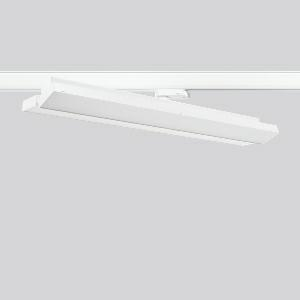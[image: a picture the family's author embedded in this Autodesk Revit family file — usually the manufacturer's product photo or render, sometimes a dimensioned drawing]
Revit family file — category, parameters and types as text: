
# Revit family: tx-move_742164_002_cd2c
name_source: partatom
category: Lighting Fixtures
units: mm (PartAtom-declared; Revit-internal decimal feet)

## family parameters
Cut with Voids When Loaded = No
Host = Face
Light Source = No
Part Type = Normal
Room Calculation Point = No
Round Connector Dimension = Use Diameter
Shared = No

## types (1)
- MultiLumen 1 (1 x LED Modul 830, 2450 lm, 3000)
    Apparent Load = 41 VA
    CIE Flux Codes = 47 79 96 100 100
    Color Rendering = 80
    Color Temperature = 3000
    Default Elevation = 1800 mm
    Description = Series: TX-MOVE
Multifunctional surface-mounted spotlight for area lighting. Very flat design. Housing: sheet steel, powder-coated. Rotation range: 356°. Swivel range: 90°. Consistent alignment possible with visible tilt scale. High-efficiency LED units with flush-mounted opal diffuser made of non-yellowing PMMA. Symmetrical wide beam light emission. With multi adaptor for 3-circuit tracks 230 V. Suitable for Track on ceiling. MultiLumen: Luminous flux adjustable in 3 steps. Factory setting is the highest luminous flux. Environmentally friendly and resource-saving due to replaceable and recyclable components. 
Colour: traffic white, matt (RAL 9016)
Length: 570 mm
Width: 119 mm
Height: 92 mm
Lamp: LED
Socket: without socket
Colour temperature: 3000K
Colour rendering index (CRI): 80
System power: 41 W
Rated luminous flux: 4900 lm
Luminous efficiency: 120 lm/W
System power 2: 57 W
Rated luminous flux 2: 6650 lm
Luminous efficiency 2: 117 lm/W
System power 3: 73 W
Rated luminous flux 3: 8150 lm
Luminous efficiency 3: 112 lm/W
Control gear: Regulated power supply
Protection class: I
Type of protection: IP 20
    Height = 75 mm
    Lamp = 1 x LED Modul 830
    Lamp Light Flux = 2450 lm
    Lamp count = 1
    Length = 569 mm
    Lifetime = 50000 h
    Luminous efficacy = 120 lm/W
    Manufacturer = RZB
    ModVariant = No
    Model = 742164.002
    Mounting Place = Ceiling
    Mounting Type = Surface mounted
    Number of Poles = 1
    OnlyDefault = Yes
    Power Factor = 1
    Product Name = TX-MOVE
    Product group = Track mounted projectors
    ProductGroupID = 301
    Protection Class = Protection class I
    Protection Degree = IP 20
    RLX_Detail_Level = 1
    RLX_Emergency_Light_Flux = 0 lm
    RLX_Emergency_Type = 0
    RLX_Emergency_Type_DB = No
    RlxData = <blob elided: 29825 chars, md5=96a3f4c9>
    Socket = socket
    Standby Power = 0 W
    System Light Flux = 4900 lm
    System Power = 41 W
    Type Comments = MultiLumen 1
    Type Image = 742164.002.jpg
    URL = http://relux.com
    VarID = multilumen_1
    Voltage = 0 V
    Weight = 0.00 kg
    Width = 119 mm

## geometry (parser evidence)
native form markers: Blend x4, Sweep x15
no freeform markers — native parametric forms only
